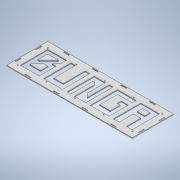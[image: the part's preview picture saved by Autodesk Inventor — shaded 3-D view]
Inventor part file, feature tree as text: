
AUTODESK INVENTOR PART (.ipt)
format: ipt  version: 2022 (Build 260153000, 153)  size: 349,184 bytes
history: native  units: in
note: dims shown in document units (in); Inventor stores cm internally (conversion verified against a paired STEP export)
features: extrude x1, sketch x1
ambient origin geometry x8: Origin, YZ Plane, XZ Plane, XY Plane, X Axis, Y Axis, Z Axis, Center Point
bodies: Body1 (feature_tree)
feature tree (2):
  extrude  "Extrusion2"  Depth=0.1181in
  sketch  "Sketch1"  dims[d0=20.0in d1=12.0in d2=19.685in d3=11.811in d6=2.7559in d7=4.0157in d8=1.1811in d10=3.4252in d11=1.1811in d13=3.4252in d16=135.0deg d17=135.0deg d18=0.5512in d19=0.5512in d20=0.5906in d21=0.7874in d22=0.5906in d23=0.5906in d24=0.7874in d25=0.5906in d26=0.5906in d27=0.4331in d28=0.5906in d29=0.8268in d30=0.8268in d31=0.5512in d32=0.7874in d33=0.5906in d34=0.6693in d35=0.7874in d36=0.6693in d38=0.5512in d43=0.0in d45=0.5906in d47=135.0deg d49=0.5906in d51=135.0deg d56=0.7874in d57=45.0deg d58=0.5906in d59=0.5906in d60=0.1181in d61=0.0in d62=45.0deg d63=18.5039in d64=0.5906in d67=6.063in d68=16.4567in d69=4.0157in d70=0.5512in d71=0.1457in d72=0.1969in d73=0.1969in d74=4.2126in d75=4.2126in d76=4.2126in d77=4.2126in d78=0.1181in d79=0.7874in d80=0.1181in d81=6.3189in d82=0.7874in d83=0.1181in d84=0.1181in d85=1.5748in d87=4.2126in d88=0.3937in d90=0.3937in d92=0.1181in d93=0.7874in d94=1.5157in d95=0.1181in d96=0.1181in d97=0.7874in d98=0.1181in d99=1.5157in d100=0.1181in d101=0.7874in d102=0.1181in d103=0.7874in d104=0.1181in]
